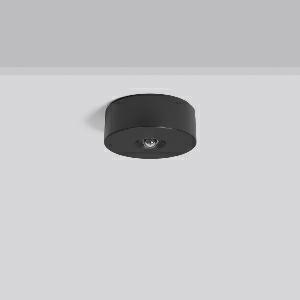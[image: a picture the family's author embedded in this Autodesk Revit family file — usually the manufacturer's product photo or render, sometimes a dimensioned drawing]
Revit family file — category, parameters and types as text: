
# Revit family: lucio_2_672529_003_f021
name_source: partatom
category: Lighting Fixtures
units: mm (PartAtom-declared; Revit-internal decimal feet)

## family parameters
Cut with Voids When Loaded = No
Host = Face
Light Source = No
Part Type = Normal
Room Calculation Point = No
Round Connector Dimension = Use Diameter
Shared = No

## types (1)
- Flaechenlinse (1 x LED Modul 740, 310 lm, 4000)
    Apparent Load = 4 VA
    CIE Flux Codes = 44 87 99 100 100
    Color Rendering = 70
    Color Temperature = 4000
    Default Elevation = 1800 mm
    Description = Series: LUCIO 2
Round surface-mounted downlight. For escape route illumination. Housing: plastic (polycarbonate). Cover: polycarbonate. Plastic lenses for area lighting and escape route illumination included in scope of delivery. Suitable for Ceiling mounting. Suitable for connection to central battery systems. 
Colour: black
Diameter: 110 mm
Height: 46 mm
Weight: 0.16 kg
Operating mode: non-maintained power mode
Lamp: LED
Socket: without socket
Colour temperature: 4000K
Colour rendering index (CRI): 70
Luminous flux, emergency: 310 lm
System power, emergency: 4.6 W
Luminous flux, emergency 2: 290 lm
System power, emergency 2: 4.6 W
Control gear: EB
Protection class: II
Type of protection: IP 20
    Height = 46 mm
    Lamp = 1 x LED Modul 740
    Lamp Light Flux = 310 lm
    Lamp count = 1
    Length = 110 mm
    Lifetime = 50000 h
    Luminous efficacy = 74 lm/W
    Manufacturer = RZB
    ModVariant = No
    Model = 672529.003
    Mounting Place = Ceiling
    Mounting Type = Surface mounted
    Number of Poles = 1
    OnlyDefault = Yes
    Power Factor = 1
    Product Name = LUCIO 2
    Product group = Surface mounted ceiling luminaires
    ProductGroupID = 303
    Protection Class = Protection class II
    Protection Degree = Degree of protection
    RLX_Detail_Level = 1
    RLX_Emergency_Light_Flux = 310 lm
    RLX_Emergency_Type = 3
    RLX_Emergency_Type_DB = Yes
    RlxData = <blob elided: 168053 chars, md5=24cb29e5>
    Socket = socket
    Standby Power = 0 W
    System Light Flux = 310 lm
    System Power = 4 W
    Type Comments = Area lens
    Type Image = 672527.003.jpg
    URL = http://relux.com
    VarID = flaechenlinse
    Voltage = 0 V
    Weight = 0.00 kg
    Width = 0 mm  [stored 0 ft]

note: [stored X ft] marks values corroborated as IEEE doubles in the binary element streams (Revit-internal decimal feet)

## geometry (parser evidence)
native form markers: Blend x4, Sweep x10
no freeform markers — native parametric forms only
